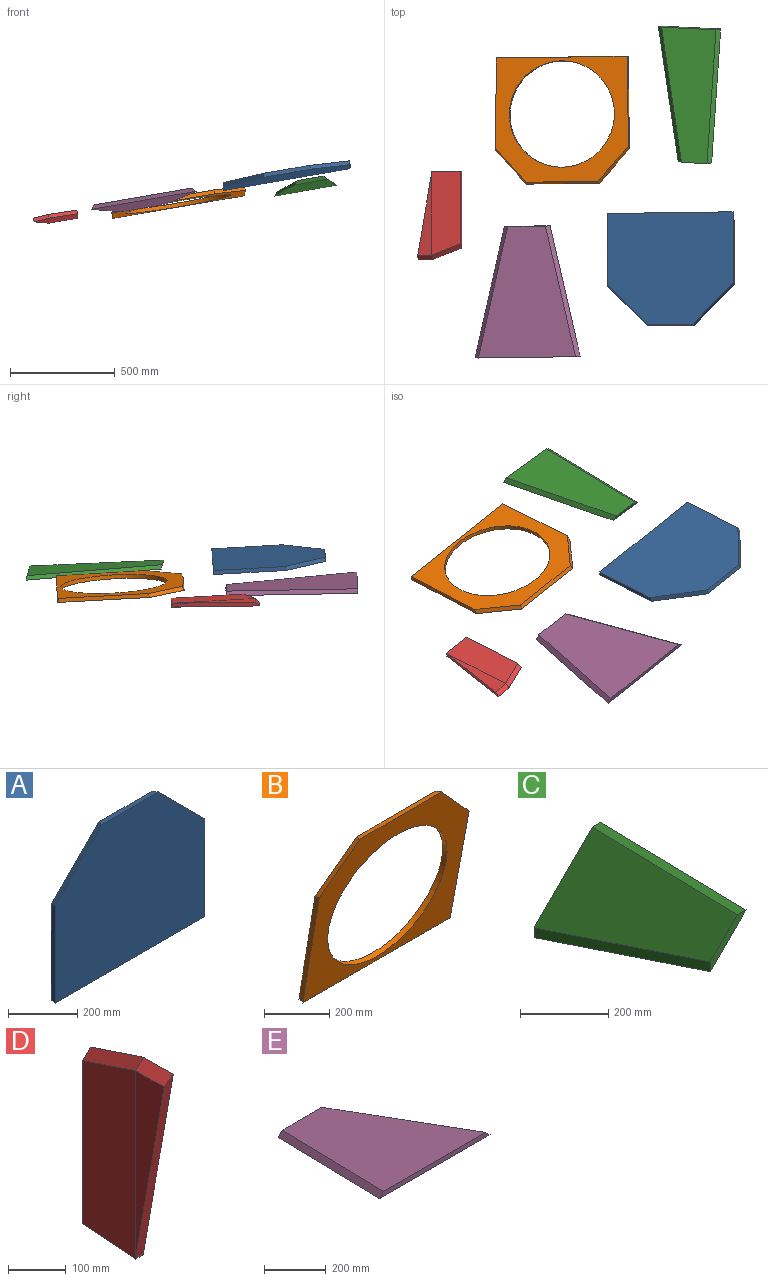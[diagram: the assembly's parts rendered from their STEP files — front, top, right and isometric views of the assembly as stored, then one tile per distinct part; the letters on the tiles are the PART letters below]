
ASSEMBLY  parts=5 mates=4
PART A: 8 faces, bbox 612.4x19.1x537.6 mm
  f0: plane 229.91x19.05mm, normal (0,0.21,0.98), area 4395.9mm2, adj f3,f4,f6,f7
  f1: plane 346.33x19.05mm, normal (-1,0.07,0), area 6545.8mm2, adj f3,f4,f5,f7
  f2: plane 346.33x19.05mm, normal (1,0.07,0), area 6545.8mm2, adj f3,f4,f5,f6
  f3: plane 612.38x537.57mm, normal (0,-1,0), area 292624.3mm2, adj f0,f1,f2,f5,f6,f7
  f4: plane 609.6x533.4mm, normal (0,1,0), area 287396.8mm2, adj f0,f1,f2,f5,f6,f7
  f5: plane 612.38x19.05mm, normal (0,0,-1), area 11639.3mm2, adj f1,f2,f3,f4
  f6: plane 198.5x195.72mm, normal (0.67,0.31,0.67), area 5455mm2, adj f0,f2,f3,f4
  f7: plane 198.5x195.72mm, normal (-0.67,0.31,0.67), area 5455mm2, adj f0,f1,f3,f4
PART B: 10 faces, bbox 646.7x123.5x595.3 mm
  f0: plane 643.72x586.28mm, normal (0,0.98,0.17), area 153508.3mm2, adj f2,f3,f4,f5,f6,f8,f9
  f1: plane 646.75x595.25mm, normal (0,-0.98,-0.17), area 162114.8mm2, adj f2,f3,f4,f5,f6,f7,f9
  f2: plane 436.19x95.45mm, normal (-1,0.07,0), area 8296.5mm2, adj f0,f1,f6,f7,f8
  f3: plane 436.19x95.45mm, normal (1,0.07,0), area 8296.5mm2, adj f0,f1,f5,f7,f8
  f4: plane 354.09x20.12mm, normal (0,0.21,0.98), area 7195.2mm2, adj f0,f1,f5,f6
  f5: plane 166.97x151.06mm, normal (0.67,0.31,0.67), area 4620.8mm2, adj f0,f1,f3,f4
  f6: plane 166.97x151.06mm, normal (-0.67,0.31,0.67), area 4620.7mm2, adj f0,f1,f2,f4
  f7: plane 635.53x4.57mm, normal (0,1,0), area 2905.6mm2, adj f1,f2,f3,f8
  f8: plane 635.53x18.54mm, normal (0,0,-1), area 11756.2mm2, adj f0,f2,f3,f7
  f9: cylinder r=254mm len=508mm, axis (0,-0.98,-0.17), area 30402.4mm2, adj f0,f1
PART C: 6 faces, bbox 257.8x609.6x346.7 mm
  f0: plane 114.3x114.3mm, normal (0,-1,0), area 2716.4mm2, adj f2,f3,f4,f5
  f1: plane 213.38x213.38mm, normal (0,1,0), area 5385.7mm2, adj f2,f3,f4,f5
  f2: plane 609.6x346.73mm, normal (0.67,-0.31,-0.67), area 148352.8mm2, adj f0,f1,f3,f5
  f3: plane 609.6x259.37mm, normal (-1,0.07,0), area 16466.7mm2, adj f0,f1,f2,f4
  f4: plane 609.6x319.79mm, normal (-0.67,0.31,0.67), area 123958.6mm2, adj f0,f1,f3,f5
  f5: plane 609.6x170.47mm, normal (0,0.21,0.98), area 16811.4mm2, adj f0,f1,f2,f4
PART D: 10 faces, bbox 29.3x213.3x418.9 mm
  f0: plane 19.1x4.57mm, normal (0,-1,0), area 87.3mm2, adj f2,f3,f5,f6
  f1: plane 140.21x72.56mm, normal (-0.67,0.31,0.67), area 3978mm2, adj f2,f4,f5,f7
  f2: plane 418.9x140.21mm, normal (1,-0.07,0), area 55132.3mm2, adj f0,f1,f3,f4,f9
  f3: plane 140.21x29.32mm, normal (0,0,-1), area 2678.1mm2, adj f0,f2,f4,f5
  f4: plane 365.43x19.1mm, normal (0,1,0), area 6797.6mm2, adj f1,f2,f3,f5
  f5: plane 399.79x140.21mm, normal (-1,0.07,0), area 52447.1mm2, adj f0,f1,f3,f4,f8
  f6: plane 414.32x73.06mm, normal (0,-0.98,-0.17), area 7850.7mm2, adj f0,f7,f8,f9
  f7: plane 73.06x19.1mm, normal (-0.71,0,0.71), area 1927.9mm2, adj f1,f6,f8,f9
  f8: plane 395.22x69.69mm, normal (-1,0,0), area 13771.2mm2, adj f5,f6,f7
  f9: plane 414.32x73.06mm, normal (1,0,0), area 15134.5mm2, adj f2,f6,f7
PART E: 6 faces, bbox 508x609.6x152.4 mm
  f0: plane 508x19.05mm, normal (0,-1,0), area 9314.5mm2, adj f2,f3,f4,f5
  f1: plane 220.94x19.05mm, normal (0,1,0), area 3846mm2, adj f2,f3,f4,f5
  f2: plane 609.6x469.9mm, normal (0,0.21,0.98), area 203660.2mm2, adj f0,f1,f3,f5
  f3: plane 609.6x162.58mm, normal (0.67,0.31,0.67), area 17249.3mm2, adj f0,f1,f2,f4
  f4: plane 609.6x508mm, normal (0,-0.21,-0.98), area 227435.1mm2, adj f0,f1,f3,f5
  f5: plane 609.6x162.58mm, normal (-0.67,0.31,0.67), area 17249.3mm2, adj f0,f1,f2,f4
PLACE A rot(axis=(0.99,-0.08,0.09),87.2deg) t=(-411.19,-977.52,-232.05)mm
PLACE B rot(axis=(0.99,-0.1,0.09),77.3deg) t=(-955.75,-300.01,-196.3)mm
PLACE C rot(axis=(0.38,0.92,0.12),37.6deg) t=(-513.57,-526.61,-323.29)mm
PLACE D rot(axis=(0.66,0.52,-0.55),110deg) t=(-2012.3,-772.84,-255.3)mm
PLACE E rot(axis=(0.68,-0.73,0.11),13.4deg) t=(-1083.5,-1524.43,-398.6)mm
MATE planar A.f4 <-> B.f0  axis (-0.17,0.06,0.98) through (-514.28,-1183.72,381.26)mm
MATE planar D.f2 <-> E.f2  axis (0.17,-0.06,-0.98) through (-1578.81,-944.37,164.08)mm
MATE planar B.f1 <-> E.f2  axis (0.17,-0.06,-0.98) through (-1027.46,-506.08,235.05)mm
MATE planar C.f4 <-> E.f2  axis (-0.17,0.06,0.98) through (-414.19,-347.65,332.41)mm
